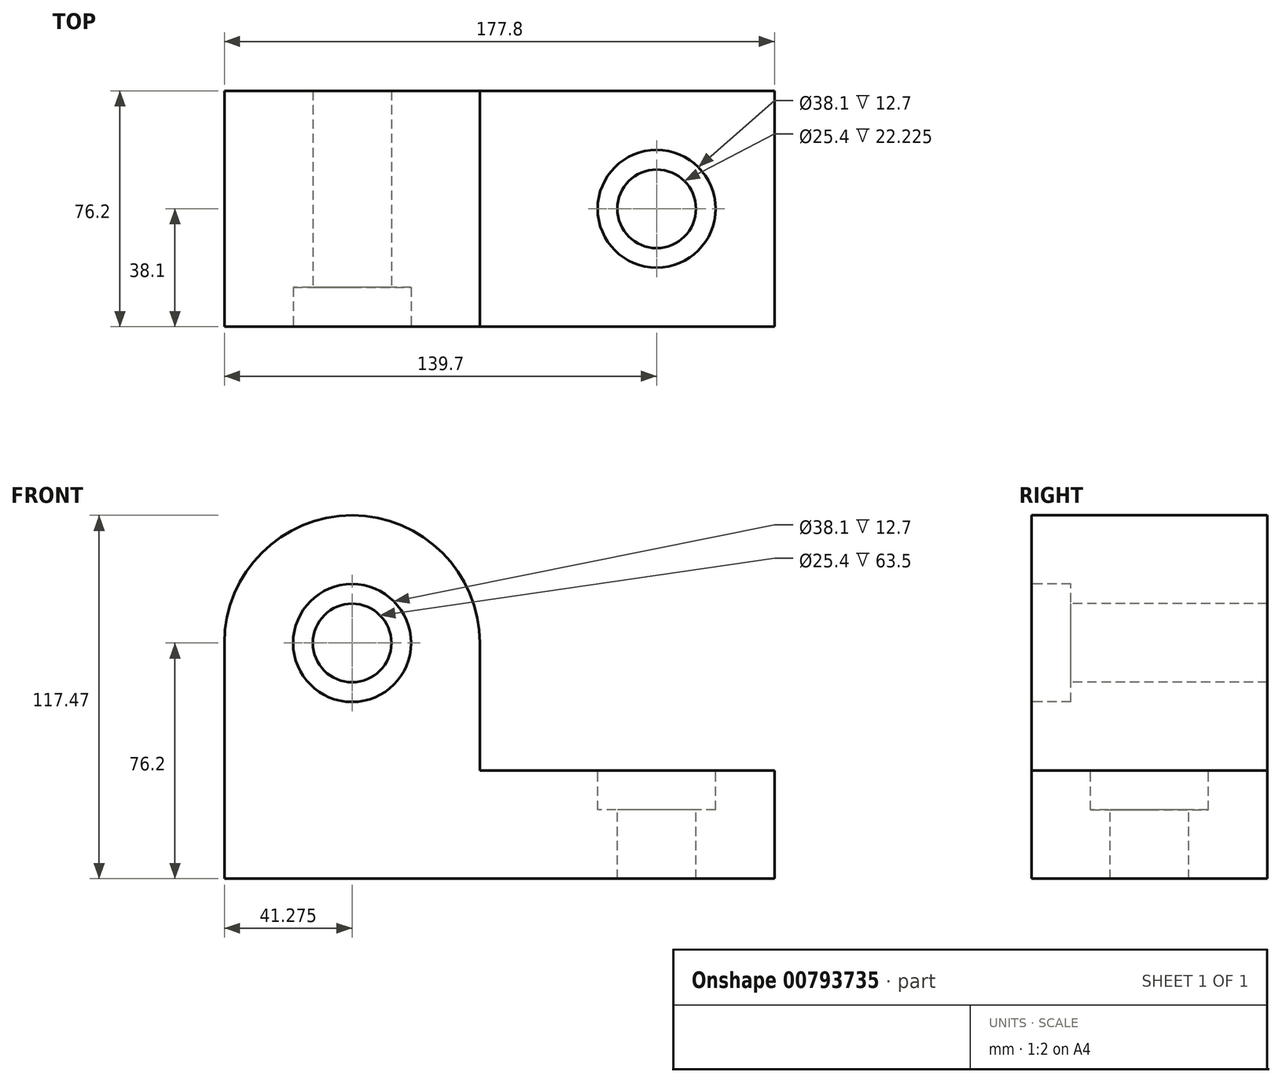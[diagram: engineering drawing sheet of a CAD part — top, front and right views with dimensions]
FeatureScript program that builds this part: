
annotation { "Feature Type Name" : "Feature", "Feature Type Description" : "" }
export const myFeature = defineFeature(function(context is Context, id is Id, definition is map)
    precondition{}
    {
        {
            var Q0;
            Q0=qCreatedBy(makeId("Front.planeOp"),FACE);
            var sketch = newSketch(context, id + "F0", { "sketchPlane" : qUnion([Q0])});
            skLineSegment(sketch, "E0", {"start": v(0, 0) * mm, "end": v(177.8, 0) * mm});
            skLineSegment(sketch, "E1", {"start": v(0, 0) * mm, "end": v(0, 34.93) * mm});
            skLineSegment(sketch, "E2", {"start": v(0, 34.93) * mm, "end": v(177.8, 34.93) * mm});
            skLineSegment(sketch, "E3", {"start": v(177.8, 34.93) * mm, "end": v(177.8, 0) * mm});
            skSolve(sketch);
        }
        {
            var Q0;
            Q0=makeQuery(id+"F0.imprint","IMPRINT",FACE,{"disambiguationData":[TD([[makeQuery(id+"F0.imprint","IMPRINT",EDGE,{"derivedFrom":sQuery(id+"F0.wireOp",EDGE,"E0")}),1.0]])]});
            extrude(context, id + "F1", {"entities" : qUnion([Q0]), "depth" : 76.2 * mm, "offsetDistance" : 25.4 * mm});
        }
        {
            var Q0;
            Q0=makeQuery(id+"F1.opExtrude","SWEPT_FACE",FACE,{"disambiguationData":[OSD([sQuery(id+"F0.wireOp",EDGE,"E2")])]});
            var sketch = newSketch(context, id + "F2", { "sketchPlane" : qUnion([Q0])});
            skLineSegment(sketch, "E4", {"start": v(82.55, 0) * mm, "end": v(82.55, -76.2) * mm});
            skSolve(sketch);
        }
        {
            var Q0;
            {var subQ0=sQuery(id+"F2.wireOp",EDGE,"E4");Q0=makeQuery(id+"F2.imprint","IMPRINT",FACE,{"disambiguationData":[TD([[makeQuery(id+"F2.imprint","IMPRINT",EDGE,{"derivedFrom":subQ0}),-1.0]])]});}
            extrude(context, id + "F3", {"entities" : qUnion([Q0]), "operationType" : NewBodyOperationType.ADD, "depth" : 88.9 * mm, "offsetDistance" : 25.4 * mm});
        }
        {
            var Q0;
            {var subQ0=sQuery(id+"F0.wireOp",EDGE,"E2");var subQ1=makeQuery(id+"F1.opExtrude","CAP_EDGE",EDGE,{"disambiguationData":[OSD([subQ0])],"isStart":false});var subQ2=sQuery(id+"F0.wireOp",EDGE,"E1");Q0=makeQuery(id+"F3.boolean.opBoolean","MERGE",FACE,{"derivedFrom":[makeQuery(id+"F1.opExtrude","CAP_FACE",FACE,{"disambiguationData":[OSD([sQuery(id+"F0.wireOp",EDGE,"E0"),subQ2,subQ0,sQuery(id+"F0.wireOp",EDGE,"E3")])],"isStart":false}),makeQuery(id+"F3.opExtrude","SWEPT_FACE",FACE,{"disambiguationData":[OSD([subQ0]),TDD([makeQuery(id+"F2.imprint","IMPRINT",EDGE,{"disambiguationData":[TD([[makeQuery(id+"F2.imprint","INTERSECT",VERTEX,{"derivedFrom":[subQ1,sQuery(id+"F2.wireOp",EDGE,"E4")]}),1.0]])],"derivedFrom":subQ1})])]})]});}
            var sketch = newSketch(context, id + "F4", { "sketchPlane" : qUnion([Q0])});
            skLineSegment(sketch, "E5", {"start": v(0, 0) * mm, "end": v(0, 76.2) * mm, "construction": true});
            skLineSegment(sketch, "E6", {"start": v(0, 76.2) * mm, "end": v(82.55, 76.2) * mm, "construction": true});
            skArc(sketch, "E7", {"start": v(82.55, 76.2) * mm, "mid": v(41.28, 117.48) * mm, "end": v(0, 76.2) * mm});
            skSolve(sketch);
        }
        {
            var Q0;
            {var subQ0=sQuery(id+"F4.wireOp",EDGE,"E7");Q0=makeQuery(id+"F4.imprint","IMPRINT",FACE,{"disambiguationData":[TD([[makeQuery(id+"F4.imprint","IMPRINT",EDGE,{"derivedFrom":subQ0}),-1.0]])]});}
            extrude(context, id + "F5", {"entities" : qUnion([Q0]), "operationType" : NewBodyOperationType.REMOVE, "endBound" : BoundingType.THROUGH_ALL, "oppositeDirection" : true, "depth" : 25.4 * mm, "offsetDistance" : 25.4 * mm});
        }
        {
            var Q0;
            Q0=makeQuery(id+"F1.opExtrude","SWEPT_FACE",FACE,{"disambiguationData":[OSD([sQuery(id+"F0.wireOp",EDGE,"E2")])]});
            var sketch = newSketch(context, id + "F6", { "sketchPlane" : qUnion([Q0])});
            skLineSegment(sketch, "E8", {"start": v(177.8, -38.1) * mm, "end": v(139.7, -38.1) * mm, "construction": true});
            skCircle(sketch, "E9", {"center": v(139.7, -38.1) * mm, "radius": 19.05 * mm});
            skSolve(sketch);
        }
        {
            var Q0;
            Q0=makeQuery(id+"F6.imprint","IMPRINT",FACE,{"disambiguationData":[TD([[makeQuery(id+"F6.imprint","IMPRINT",EDGE,{"derivedFrom":sQuery(id+"F6.wireOp",EDGE,"E9")}),1.0]])]});
            extrude(context, id + "F7", {"entities" : qUnion([Q0]), "operationType" : NewBodyOperationType.REMOVE, "oppositeDirection" : true, "depth" : 12.7 * mm, "offsetDistance" : 25.4 * mm});
        }
        {
            var Q0;
            Q0=makeQuery(id+"F1.opExtrude","SWEPT_FACE",FACE,{"disambiguationData":[OSD([sQuery(id+"F0.wireOp",EDGE,"E2")])]});
            var sketch = newSketch(context, id + "F8", { "sketchPlane" : qUnion([Q0])});
            skLineSegment(sketch, "E10", {"start": v(177.8, -38.1) * mm, "end": v(139.7, -38.1) * mm, "construction": true});
            skCircle(sketch, "E11", {"center": v(139.7, -38.1) * mm, "radius": 12.7 * mm});
            skSolve(sketch);
        }
        {
            var Q0;
            Q0=makeQuery(id+"F8.imprint","IMPRINT",FACE,{"disambiguationData":[TD([[makeQuery(id+"F8.imprint","IMPRINT",EDGE,{"derivedFrom":sQuery(id+"F8.wireOp",EDGE,"E11")}),1.0]])]});
            extrude(context, id + "F9", {"entities" : qUnion([Q0]), "operationType" : NewBodyOperationType.REMOVE, "endBound" : BoundingType.THROUGH_ALL, "oppositeDirection" : true, "depth" : 25.4 * mm, "offsetDistance" : 25.4 * mm});
        }
        {
            var Q0;
            {var subQ0=sQuery(id+"F0.wireOp",EDGE,"E2");var subQ1=makeQuery(id+"F1.opExtrude","CAP_EDGE",EDGE,{"disambiguationData":[OSD([subQ0])],"isStart":false});var subQ2=sQuery(id+"F0.wireOp",EDGE,"E1");Q0=makeQuery(id+"F3.boolean.opBoolean","MERGE",FACE,{"derivedFrom":[makeQuery(id+"F1.opExtrude","CAP_FACE",FACE,{"disambiguationData":[OSD([sQuery(id+"F0.wireOp",EDGE,"E0"),subQ2,subQ0,sQuery(id+"F0.wireOp",EDGE,"E3")])],"isStart":false}),makeQuery(id+"F3.opExtrude","SWEPT_FACE",FACE,{"disambiguationData":[OSD([subQ0]),TDD([makeQuery(id+"F2.imprint","IMPRINT",EDGE,{"disambiguationData":[TD([[makeQuery(id+"F2.imprint","INTERSECT",VERTEX,{"derivedFrom":[subQ1,sQuery(id+"F2.wireOp",EDGE,"E4")]}),1.0]])],"derivedFrom":subQ1})])]})]});}
            var sketch = newSketch(context, id + "F10", { "sketchPlane" : qUnion([Q0])});
            skLineSegment(sketch, "E12", {"start": v(0, 76.2) * mm, "end": v(82.55, 76.2) * mm, "construction": true});
            skLineSegment(sketch, "E13", {"start": v(41.28, 117.48) * mm, "end": v(41.28, 76.2) * mm, "construction": true});
            skCircle(sketch, "E14", {"center": v(41.28, 76.2) * mm, "radius": 19.05 * mm});
            skSolve(sketch);
        }
        {
            var Q0;
            Q0=makeQuery(id+"F10.imprint","IMPRINT",FACE,{"disambiguationData":[TD([[makeQuery(id+"F10.imprint","IMPRINT",EDGE,{"derivedFrom":sQuery(id+"F10.wireOp",EDGE,"E14")}),1.0]])]});
            extrude(context, id + "F11", {"entities" : qUnion([Q0]), "operationType" : NewBodyOperationType.REMOVE, "oppositeDirection" : true, "depth" : 12.7 * mm, "offsetDistance" : 25.4 * mm});
        }
        {
            var Q0;
            {var subQ0=sQuery(id+"F0.wireOp",EDGE,"E2");var subQ1=makeQuery(id+"F1.opExtrude","CAP_EDGE",EDGE,{"disambiguationData":[OSD([subQ0])],"isStart":false});var subQ2=sQuery(id+"F0.wireOp",EDGE,"E1");Q0=makeQuery(id+"F3.boolean.opBoolean","MERGE",FACE,{"derivedFrom":[makeQuery(id+"F1.opExtrude","CAP_FACE",FACE,{"disambiguationData":[OSD([sQuery(id+"F0.wireOp",EDGE,"E0"),subQ2,subQ0,sQuery(id+"F0.wireOp",EDGE,"E3")])],"isStart":false}),makeQuery(id+"F3.opExtrude","SWEPT_FACE",FACE,{"disambiguationData":[OSD([subQ0]),TDD([makeQuery(id+"F2.imprint","IMPRINT",EDGE,{"disambiguationData":[TD([[makeQuery(id+"F2.imprint","INTERSECT",VERTEX,{"derivedFrom":[subQ1,sQuery(id+"F2.wireOp",EDGE,"E4")]}),1.0]])],"derivedFrom":subQ1})])]})]});}
            var sketch = newSketch(context, id + "F12", { "sketchPlane" : qUnion([Q0])});
            skLineSegment(sketch, "E15", {"start": v(0, 76.2) * mm, "end": v(82.55, 76.2) * mm, "construction": true});
            skLineSegment(sketch, "E16", {"start": v(41.28, 117.48) * mm, "end": v(41.28, 76.2) * mm, "construction": true});
            skCircle(sketch, "E17", {"center": v(41.28, 76.2) * mm, "radius": 12.7 * mm});
            skSolve(sketch);
        }
        {
            var Q0;
            Q0=makeQuery(id+"F12.imprint","IMPRINT",FACE,{"disambiguationData":[TD([[makeQuery(id+"F12.imprint","IMPRINT",EDGE,{"derivedFrom":sQuery(id+"F12.wireOp",EDGE,"E17")}),1.0]])]});
            extrude(context, id + "F13", {"entities" : qUnion([Q0]), "operationType" : NewBodyOperationType.REMOVE, "endBound" : BoundingType.THROUGH_ALL, "oppositeDirection" : true, "depth" : 25.4 * mm, "offsetDistance" : 25.4 * mm});
        }
    });
